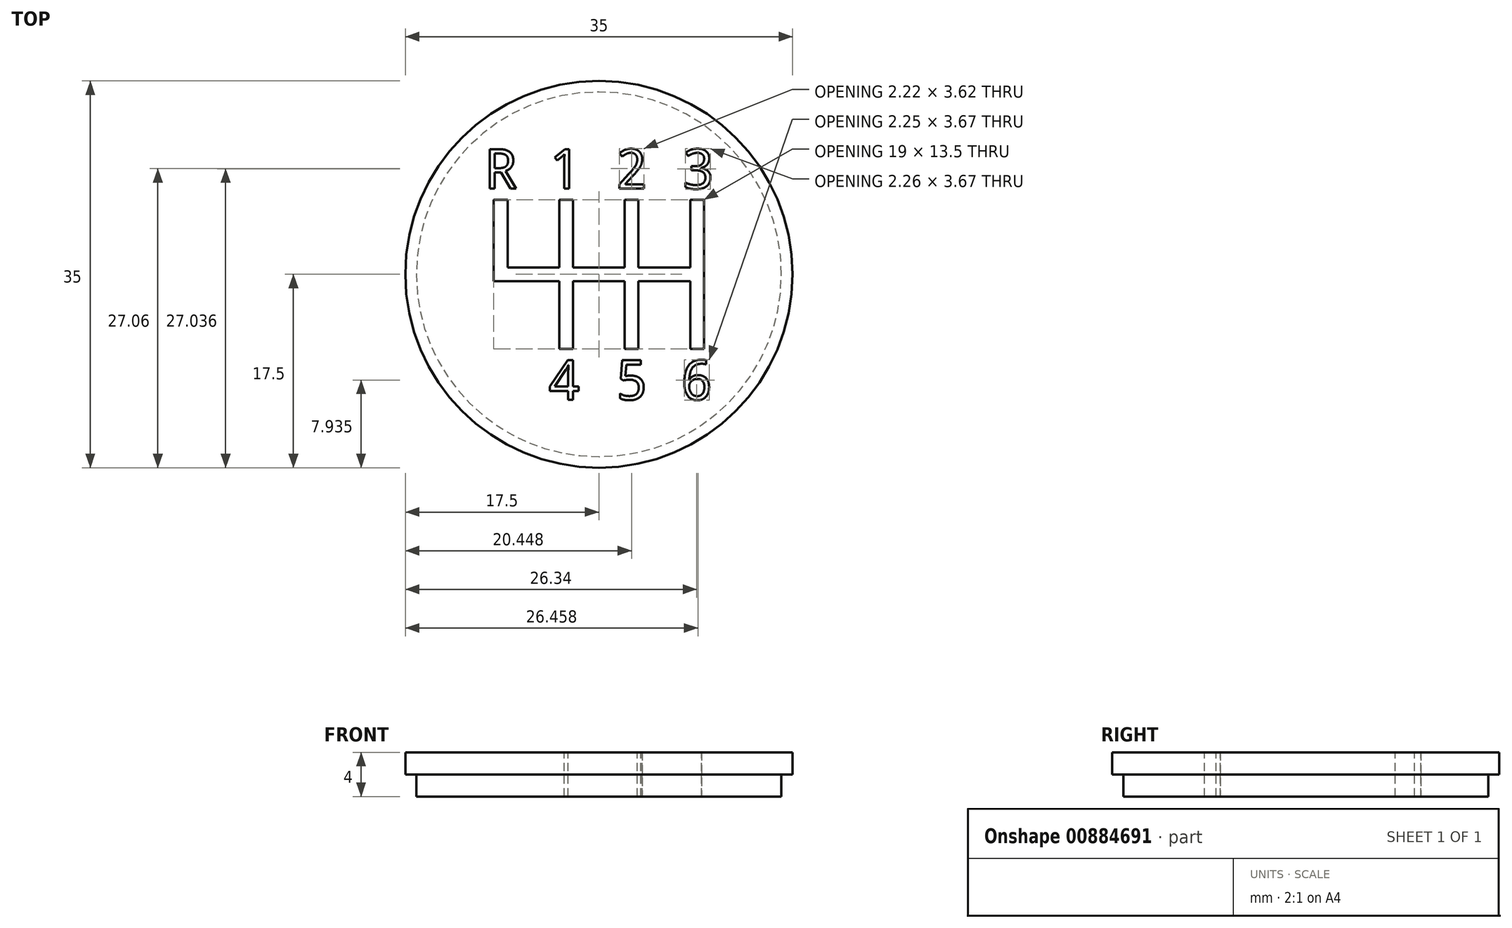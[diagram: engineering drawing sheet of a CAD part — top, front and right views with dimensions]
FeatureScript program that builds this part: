
annotation { "Feature Type Name" : "Feature", "Feature Type Description" : "" }
export const myFeature = defineFeature(function(context is Context, id is Id, definition is map)
    precondition{}
    {
        {
            var Q0;
            Q0=qCreatedBy(makeId("Top.planeOp"),FACE);
            var sketch = newSketch(context, id + "F0", { "sketchPlane" : qUnion([Q0])});
            skCircle(sketch, "E0", {"center": v(0, 0) * mm, "radius": 17.5 * mm});
            skCircle(sketch, "E1", {"center": v(0, 0) * mm, "radius": 16.5 * mm});
            skSolve(sketch);
        }
        {
            var Q0;
            Q0=makeQuery(id+"F0.imprint","IMPRINT",FACE,{"disambiguationData":[TD([[makeQuery(id+"F0.imprint","IMPRINT",EDGE,{"derivedFrom":sQuery(id+"F0.wireOp",EDGE,"E1")}),1.0]])]});
            extrude(context, id + "F1", {"entities" : qUnion([Q0]), "oppositeDirection" : true, "depth" : 4 * mm, "offsetDistance" : 25 * mm});
        }
        {
            var Q0;
            Q0=makeQuery(id+"F0.imprint","IMPRINT",FACE,{"disambiguationData":[TD([[makeQuery(id+"F0.imprint","IMPRINT",EDGE,{"derivedFrom":sQuery(id+"F0.wireOp",EDGE,"E0")}),1.0]])]});
            extrude(context, id + "F2", {"entities" : qUnion([Q0]), "operationType" : NewBodyOperationType.ADD, "oppositeDirection" : true, "depth" : 2 * mm, "offsetDistance" : 25 * mm});
        }
        {
            var Q0;
            {var subQ0=sQuery(id+"F0.wireOp",EDGE,"E1");Q0=makeQuery(id+"F2.boolean.opBoolean","MERGE",FACE,{"derivedFrom":[makeQuery(id+"F1.opExtrude","CAP_FACE",FACE,{"disambiguationData":[OSD([subQ0])],"isStart":true}),makeQuery(id+"F2.opExtrude","CAP_FACE",FACE,{"disambiguationData":[OSD([sQuery(id+"F0.wireOp",EDGE,"E0"),subQ0])],"isStart":true})]});}
            var sketch = newSketch(context, id + "F3", { "sketchPlane" : qUnion([Q0])});
            skLineSegment(sketch, "E2.bottom", {"start": v(12, 11) * mm, "end": v(-12, 11) * mm, "construction": true});
            skLineSegment(sketch, "E2.top", {"start": v(12, -11) * mm, "end": v(-12, -11) * mm, "construction": true});
            skLineSegment(sketch, "E2.left", {"start": v(12, 11) * mm, "end": v(12, -11) * mm, "construction": true});
            skLineSegment(sketch, "E2.right", {"start": v(-12, 11) * mm, "end": v(-12, -11) * mm, "construction": true});
            skPoint(sketch, "E3", {"position": v(0, 11) * mm});
            skPoint(sketch, "E4", {"position": v(12, 0) * mm});
            skLineSegment(sketch, "E5.top", {"start": v(9.5, 6.75) * mm, "end": v(8.25, 6.75) * mm});
            skLineSegment(sketch, "E5.left", {"start": v(9.5, 0.63) * mm, "end": v(9.5, 6.75) * mm});
            skLineSegment(sketch, "E5.right", {"start": v(8.25, 0.63) * mm, "end": v(8.25, 6.75) * mm});
            skLineSegment(sketch, "E6.bottom", {"start": v(8.25, 0.62) * mm, "end": v(3.58, 0.62) * mm});
            skLineSegment(sketch, "E6.top", {"start": v(8.25, -0.63) * mm, "end": v(3.58, -0.63) * mm});
            skLineSegment(sketch, "E6.right", {"start": v(-9.5, 0.63) * mm, "end": v(-9.5, -0.63) * mm});
            skLineSegment(sketch, "E7.bottom", {"start": v(-2.33, 6.75) * mm, "end": v(-3.58, 6.75) * mm});
            skLineSegment(sketch, "E7.top", {"start": v(-2.33, -6.75) * mm, "end": v(-3.58, -6.75) * mm});
            skLineSegment(sketch, "E7.left", {"start": v(-2.33, 6.75) * mm, "end": v(-2.33, 0.63) * mm});
            skLineSegment(sketch, "E7.right", {"start": v(-3.58, 6.75) * mm, "end": v(-3.58, 0.63) * mm});
            skLineSegment(sketch, "E8.bottom", {"start": v(3.58, 6.75) * mm, "end": v(2.33, 6.75) * mm});
            skLineSegment(sketch, "E8.top", {"start": v(3.58, -6.75) * mm, "end": v(2.33, -6.75) * mm});
            skLineSegment(sketch, "E8.left", {"start": v(3.58, 6.75) * mm, "end": v(3.58, 0.62) * mm});
            skLineSegment(sketch, "E8.right", {"start": v(2.33, 6.75) * mm, "end": v(2.33, 0.62) * mm});
            skLineSegment(sketch, "E9.bottom", {"start": v(-8.25, 6.75) * mm, "end": v(-9.5, 6.75) * mm});
            skLineSegment(sketch, "E9.left", {"start": v(-8.25, 6.75) * mm, "end": v(-8.25, 0.63) * mm});
            skLineSegment(sketch, "E9.right", {"start": v(-9.5, 6.75) * mm, "end": v(-9.5, -0.63) * mm});
            skPoint(sketch, "E10", {"position": v(0, -0.62) * mm});
            skLineSegment(sketch, "E11.trimOffspring", {"start": v(2.33, 0.62) * mm, "end": v(-2.33, 0.63) * mm});
            skLineSegment(sketch, "E12.trimOffspring", {"start": v(3.58, -0.63) * mm, "end": v(3.58, -6.75) * mm});
            skLineSegment(sketch, "E13.trimOffspring", {"start": v(2.33, -0.63) * mm, "end": v(2.33, -6.75) * mm});
            skLineSegment(sketch, "E14.trimOffspring", {"start": v(2.33, -0.62) * mm, "end": v(-2.33, -0.62) * mm});
            skLineSegment(sketch, "E15.trimOffspring", {"start": v(-3.58, -0.62) * mm, "end": v(-8.25, -0.62) * mm});
            skLineSegment(sketch, "E16.trimOffspring", {"start": v(-3.58, 0.63) * mm, "end": v(-8.25, 0.63) * mm});
            skLineSegment(sketch, "E17.trimOffspring", {"start": v(-2.33, -0.63) * mm, "end": v(-2.33, -6.75) * mm});
            skLineSegment(sketch, "E18.trimOffspring", {"start": v(-3.58, -0.63) * mm, "end": v(-3.58, -6.75) * mm});
            skLineSegment(sketch, "E19", {"start": v(9.5, 0.63) * mm, "end": v(9.5, -0.63) * mm});
            skPoint(sketch, "E20", {"position": v(9.5, 0) * mm});
            skLineSegment(sketch, "E21.top", {"start": v(8.25, -6.75) * mm, "end": v(9.5, -6.75) * mm});
            skLineSegment(sketch, "E21.left", {"start": v(8.25, -0.62) * mm, "end": v(8.25, -6.75) * mm});
            skLineSegment(sketch, "E21.right", {"start": v(9.5, -0.62) * mm, "end": v(9.5, -6.75) * mm});
            skLineSegment(sketch, "E22", {"start": v(-8.25, -0.62) * mm, "end": v(-9.5, -0.63) * mm});
            skSolve(sketch);
        }
        {
            var Q0;
            Q0 = qSketchRegion(id + "F3", true);
            extrude(context, id + "F4", {"entities" : qUnion([Q0]), "operationType" : NewBodyOperationType.REMOVE, "oppositeDirection" : true, "depth" : 25 * mm, "offsetDistance" : 25 * mm});
        }
        {
            var Q0;
            {var subQ0=sQuery(id+"F0.wireOp",EDGE,"E1");Q0=makeQuery(id+"F2.boolean.opBoolean","MERGE",FACE,{"derivedFrom":[makeQuery(id+"F1.opExtrude","CAP_FACE",FACE,{"disambiguationData":[OSD([subQ0])],"isStart":true}),makeQuery(id+"F2.opExtrude","CAP_FACE",FACE,{"disambiguationData":[OSD([sQuery(id+"F0.wireOp",EDGE,"E0"),subQ0])],"isStart":true})]});}
            var sketch = newSketch(context, id + "F5", { "sketchPlane" : qUnion([Q0])});
            skText(sketch, "E23", { "text": "R", "fontName": "DroidSansMono.ttf"});
            skText(sketch, "E24", { "text": "1", "fontName": "DroidSansMono.ttf"});
            skLineSegment(sketch, "E25", {"start": v(-4.55, 7.75) * mm, "end": v(-6.72, 7.75) * mm, "construction": true});
            skText(sketch, "E26", { "text": "2", "fontName": "DroidSansMono.ttf"});
            skText(sketch, "E27", { "text": "3", "fontName": "DroidSansMono.ttf"});
            skText(sketch, "E28", { "text": "4", "fontName": "DroidSansMono.ttf"});
            skText(sketch, "E29", { "text": "5", "fontName": "DroidSansMono.ttf"});
            skText(sketch, "E30", { "text": "6", "fontName": "DroidSansMono.ttf"});
            skLineSegment(sketch, "E31", {"start": v(-6.72, 11.35) * mm, "end": v(-4.55, 11.35) * mm, "construction": true});
            skLineSegment(sketch, "E32", {"start": v(-1.95, 11.35) * mm, "end": v(1.45, 11.35) * mm, "construction": true});
            skLineSegment(sketch, "E33", {"start": v(-1.95, 7.75) * mm, "end": v(1.45, 7.75) * mm, "construction": true});
            skLineSegment(sketch, "E34", {"start": v(4.8, 7.75) * mm, "end": v(7.51, 7.75) * mm, "construction": true});
            skLineSegment(sketch, "E35", {"start": v(4.8, 11.35) * mm, "end": v(7.51, 11.35) * mm, "construction": true});
            skLineSegment(sketch, "E36", {"start": v(-1.08, -7.75) * mm, "end": v(1.48, -7.75) * mm, "construction": true});
            skLineSegment(sketch, "E37", {"start": v(-1.08, -11.35) * mm, "end": v(1.48, -11.35) * mm, "construction": true});
            skLineSegment(sketch, "E38", {"start": v(4.8, -11.35) * mm, "end": v(7.34, -11.35) * mm, "construction": true});
            skLineSegment(sketch, "E39", {"start": v(4.8, -7.75) * mm, "end": v(7.34, -7.75) * mm, "construction": true});
            const initialGuessF5  = {"E23": [-0.01033, 0.00775, 1, 0, 0.0036], "E24": [-0.00455, 0.00775, 1, 0, 0.0036], "E26": [0.00145, 0.00775, 1, 0, 0.0036], "E27": [0.00751, 0.00775, 1, 0, 0.0036], "E28": [-0.00458, -0.01135, 1, 0, 0.0036], "E29": [0.00148, -0.01135, 1, 0, 0.0036], "E30": [0.00734, -0.01135, 1, 0, 0.0036]};
            skSetInitialGuess(sketch, initialGuessF5);
            skSolve(sketch);
        }
        {
            var Q0;
            Q0 = qSketchRegion(id + "F5", true);
            extrude(context, id + "F6", {"entities" : qUnion([Q0]), "operationType" : NewBodyOperationType.REMOVE, "oppositeDirection" : true, "depth" : 25 * mm, "offsetDistance" : 25 * mm});
        }
    });
